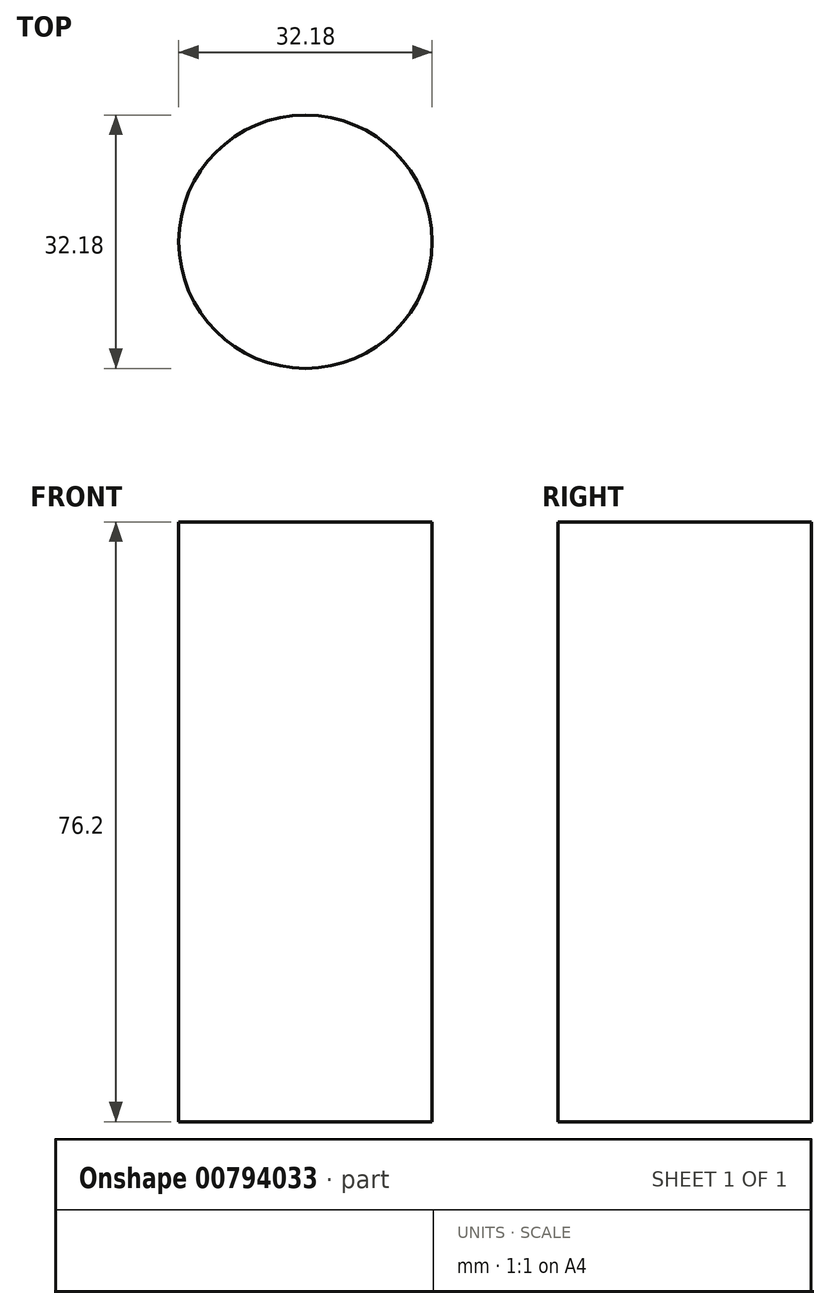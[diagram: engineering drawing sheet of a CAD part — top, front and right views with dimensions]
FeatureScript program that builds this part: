
annotation { "Feature Type Name" : "Feature", "Feature Type Description" : "" }
export const myFeature = defineFeature(function(context is Context, id is Id, definition is map)
    precondition{}
    {
        {
            var Q0;
            Q0=qCreatedBy(makeId("Top.planeOp"),FACE);
            var sketch = newSketch(context, id + "F0", { "sketchPlane" : qUnion([Q0])});
            skCircle(sketch, "E0", {"center": v(0, 0) * mm, "radius": 16.1 * mm});
            skSolve(sketch);
        }
        {
            var Q0;
            Q0 = qSketchRegion(id + "F0", true);
            extrude(context, id + "F1", {"entities" : qUnion([Q0]), "depth" : 76.2 * mm, "offsetDistance" : 25.4 * mm});
        }
    });
